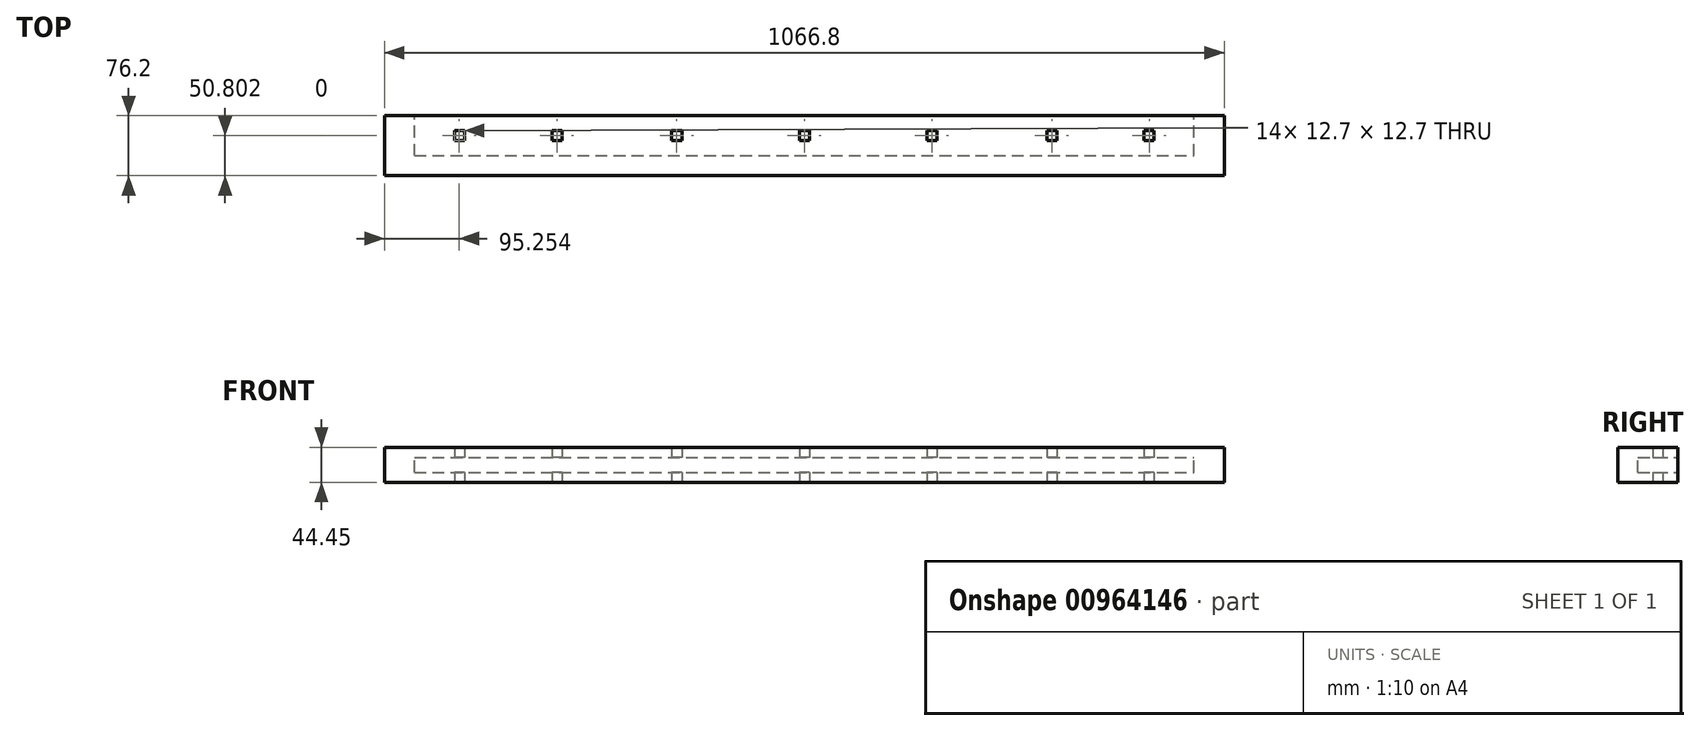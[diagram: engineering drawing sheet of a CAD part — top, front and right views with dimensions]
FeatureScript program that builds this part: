
annotation { "Feature Type Name" : "Feature", "Feature Type Description" : "" }
export const myFeature = defineFeature(function(context is Context, id is Id, definition is map)
    precondition{}
    {
        {
            var Q0;
            Q0=qCreatedBy(makeId("Top.planeOp"),FACE);
            var sketch = newSketch(context, id + "F0", { "sketchPlane" : qUnion([Q0])});
            skLineSegment(sketch, "E0.bottom", {"start": v(-127.15, 37.15) * mm, "end": v(939.65, 37.15) * mm});
            skLineSegment(sketch, "E0.top", {"start": v(-127.15, -39.05) * mm, "end": v(939.65, -39.05) * mm});
            skLineSegment(sketch, "E0.left", {"start": v(-127.15, 37.15) * mm, "end": v(-127.15, -39.05) * mm});
            skLineSegment(sketch, "E0.right", {"start": v(939.65, 37.15) * mm, "end": v(939.65, -39.05) * mm});
            skSolve(sketch);
        }
        {
            var Q0;
            Q0 = qSketchRegion(id + "F0", true);
            extrude(context, id + "F1", {"entities" : qUnion([Q0]), "depth" : 44.45 * mm, "offsetDistance" : 25.4 * mm});
        }
        {
            var Q0;
            Q0=makeQuery(id+"F1.opExtrude","SWEPT_FACE",FACE,{"disambiguationData":[OSD([sQuery(id+"F0.wireOp",EDGE,"E0.bottom")])]});
            var sketch = newSketch(context, id + "F2", { "sketchPlane" : qUnion([Q0])});
            skPoint(sketch, "E1.oppositeSnap0", {"position": v(-939.65, 22.23) * mm});
            skLineSegment(sketch, "E1.bottom", {"start": v(89.05, 12.7) * mm, "end": v(-901.55, 12.7) * mm});
            skLineSegment(sketch, "E1.top", {"start": v(89.05, 31.75) * mm, "end": v(-901.55, 31.75) * mm});
            skLineSegment(sketch, "E1.left", {"start": v(89.05, 12.7) * mm, "end": v(89.05, 31.75) * mm});
            skLineSegment(sketch, "E1.right", {"start": v(-901.55, 12.7) * mm, "end": v(-901.55, 31.75) * mm});
            skSolve(sketch);
        }
        {
            var Q0;
            Q0 = qSketchRegion(id + "F2", true);
            extrude(context, id + "F3", {"entities" : qUnion([Q0]), "operationType" : NewBodyOperationType.REMOVE, "oppositeDirection" : true, "depth" : 50.8 * mm, "offsetDistance" : 25.4 * mm});
        }
        {
            var Q0;
            Q0=makeQuery(id+"F1.opExtrude","CAP_FACE",FACE,{"disambiguationData":[OSD([sQuery(id+"F0.wireOp",EDGE,"E0.bottom"),sQuery(id+"F0.wireOp",EDGE,"E0.top"),sQuery(id+"F0.wireOp",EDGE,"E0.left"),sQuery(id+"F0.wireOp",EDGE,"E0.right")])],"isStart":true});
            var sketch = newSketch(context, id + "F4", { "sketchPlane" : qUnion([Q0])});
            skLineSegment(sketch, "E2.bottom", {"start": v(-38.25, -18.1) * mm, "end": v(-25.55, -18.1) * mm});
            skLineSegment(sketch, "E2.top", {"start": v(-38.25, -5.4) * mm, "end": v(-25.55, -5.4) * mm});
            skLineSegment(sketch, "E2.left", {"start": v(-38.25, -18.1) * mm, "end": v(-38.25, -5.4) * mm});
            skLineSegment(sketch, "E2.right", {"start": v(-25.55, -18.1) * mm, "end": v(-25.55, -5.4) * mm});
            skLineSegment(sketch, "E3.bottom", {"start": v(85.58, -18.1) * mm, "end": v(98.28, -18.1) * mm});
            skLineSegment(sketch, "E3.top", {"start": v(85.58, -5.4) * mm, "end": v(98.28, -5.4) * mm});
            skLineSegment(sketch, "E3.left", {"start": v(85.58, -18.1) * mm, "end": v(85.58, -5.4) * mm});
            skLineSegment(sketch, "E3.right", {"start": v(98.28, -18.1) * mm, "end": v(98.28, -5.4) * mm});
            skLineSegment(sketch, "E4.bottom", {"start": v(237.98, -18.1) * mm, "end": v(250.68, -18.1) * mm});
            skLineSegment(sketch, "E4.top", {"start": v(237.98, -5.4) * mm, "end": v(250.68, -5.4) * mm});
            skLineSegment(sketch, "E4.left", {"start": v(237.98, -18.1) * mm, "end": v(237.98, -5.4) * mm});
            skLineSegment(sketch, "E4.right", {"start": v(250.68, -18.1) * mm, "end": v(250.68, -5.4) * mm});
            skLineSegment(sketch, "E5.bottom", {"start": v(399.9, -18.1) * mm, "end": v(412.6, -18.1) * mm});
            skLineSegment(sketch, "E5.top", {"start": v(399.9, -5.4) * mm, "end": v(412.6, -5.4) * mm});
            skLineSegment(sketch, "E5.left", {"start": v(399.9, -18.1) * mm, "end": v(399.9, -5.4) * mm});
            skLineSegment(sketch, "E5.right", {"start": v(412.6, -18.1) * mm, "end": v(412.6, -5.4) * mm});
            skLineSegment(sketch, "E6.bottom", {"start": v(561.83, -18.1) * mm, "end": v(574.53, -18.1) * mm});
            skLineSegment(sketch, "E6.top", {"start": v(561.83, -5.4) * mm, "end": v(574.53, -5.4) * mm});
            skLineSegment(sketch, "E6.left", {"start": v(561.83, -18.1) * mm, "end": v(561.83, -5.4) * mm});
            skLineSegment(sketch, "E6.right", {"start": v(574.53, -18.1) * mm, "end": v(574.53, -5.4) * mm});
            skLineSegment(sketch, "E7.bottom", {"start": v(714.23, -18.1) * mm, "end": v(726.93, -18.1) * mm});
            skLineSegment(sketch, "E7.top", {"start": v(714.23, -5.4) * mm, "end": v(726.93, -5.4) * mm});
            skLineSegment(sketch, "E7.left", {"start": v(714.23, -18.1) * mm, "end": v(714.23, -5.4) * mm});
            skLineSegment(sketch, "E7.right", {"start": v(726.93, -18.1) * mm, "end": v(726.93, -5.4) * mm});
            skLineSegment(sketch, "E8.bottom", {"start": v(838.05, -18.1) * mm, "end": v(850.75, -18.1) * mm});
            skLineSegment(sketch, "E8.top", {"start": v(838.05, -5.4) * mm, "end": v(850.75, -5.4) * mm});
            skLineSegment(sketch, "E8.left", {"start": v(850.75, -18.1) * mm, "end": v(850.75, -5.4) * mm});
            skLineSegment(sketch, "E8.right", {"start": v(838.05, -18.1) * mm, "end": v(838.05, -5.4) * mm});
            skSolve(sketch);
        }
        {
            var Q0;
            Q0 = qSketchRegion(id + "F4", true);
            extrude(context, id + "F5", {"entities" : qUnion([Q0]), "operationType" : NewBodyOperationType.REMOVE, "endBound" : BoundingType.THROUGH_ALL, "oppositeDirection" : true, "depth" : 25.4 * mm, "offsetDistance" : 25.4 * mm});
        }
    });
